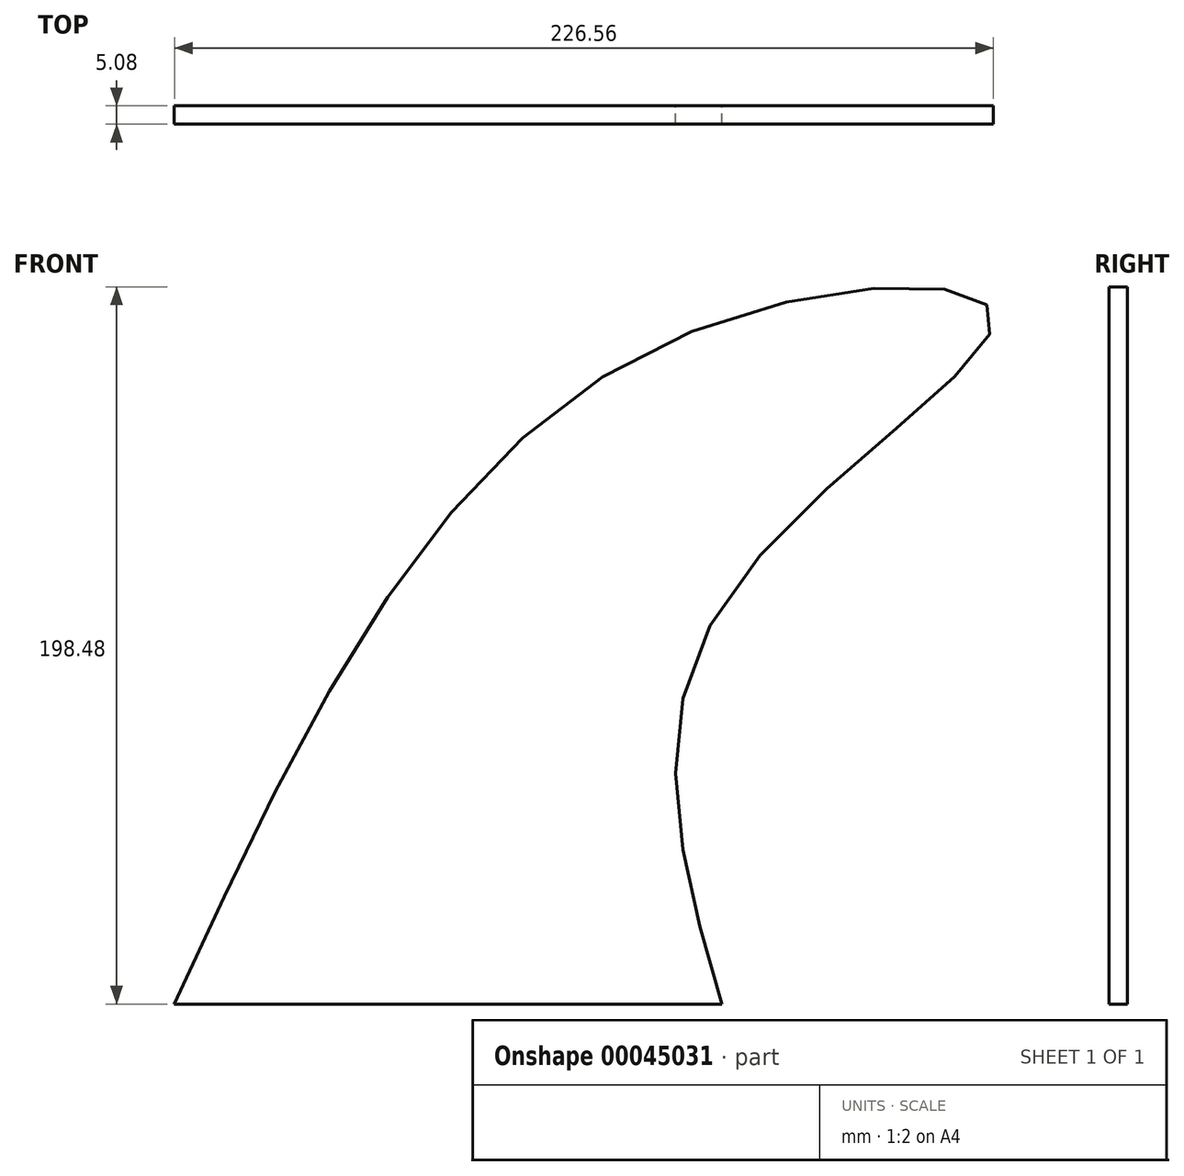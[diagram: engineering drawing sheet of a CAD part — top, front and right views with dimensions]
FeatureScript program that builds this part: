
annotation { "Feature Type Name" : "Feature", "Feature Type Description" : "" }
export const myFeature = defineFeature(function(context is Context, id is Id, definition is map)
    precondition{}
    {
        {
            var Q0;
            Q0=qCreatedBy(makeId("Front.planeOp"),FACE);
            var sketch = newSketch(context, id + "F0", { "sketchPlane" : qUnion([Q0])});
            skLineSegment(sketch, "E0", {"start": v(-75.3, -75.5) * mm, "end": v(76.1, -75.5) * mm});
            skFitSpline(sketch, "E1", {"points": [v(76.1, -75.5) * mm, v(76.1, 34.8) * mm, v(151.2, 114.77) * mm, v(55.35, 105) * mm, v(-75.3, -75.5) * mm], "startDerivative": vector(-145.04, 493.93) * mm, "endDerivative": vector(-315.04, -684.4) * mm});
            skSolve(sketch);
        }
        {
            var Q0;
            Q0=makeQuery(id+"F0.imprint","IMPRINT",FACE,{"disambiguationData":[TD([[makeQuery(id+"F0.imprint","IMPRINT",EDGE,{"derivedFrom":sQuery(id+"F0.wireOp",EDGE,"E0")}),1.0]])]});
            extrude(context, id + "F1", {"entities" : qUnion([Q0]), "depth" : 5.08 * mm});
        }
    });
